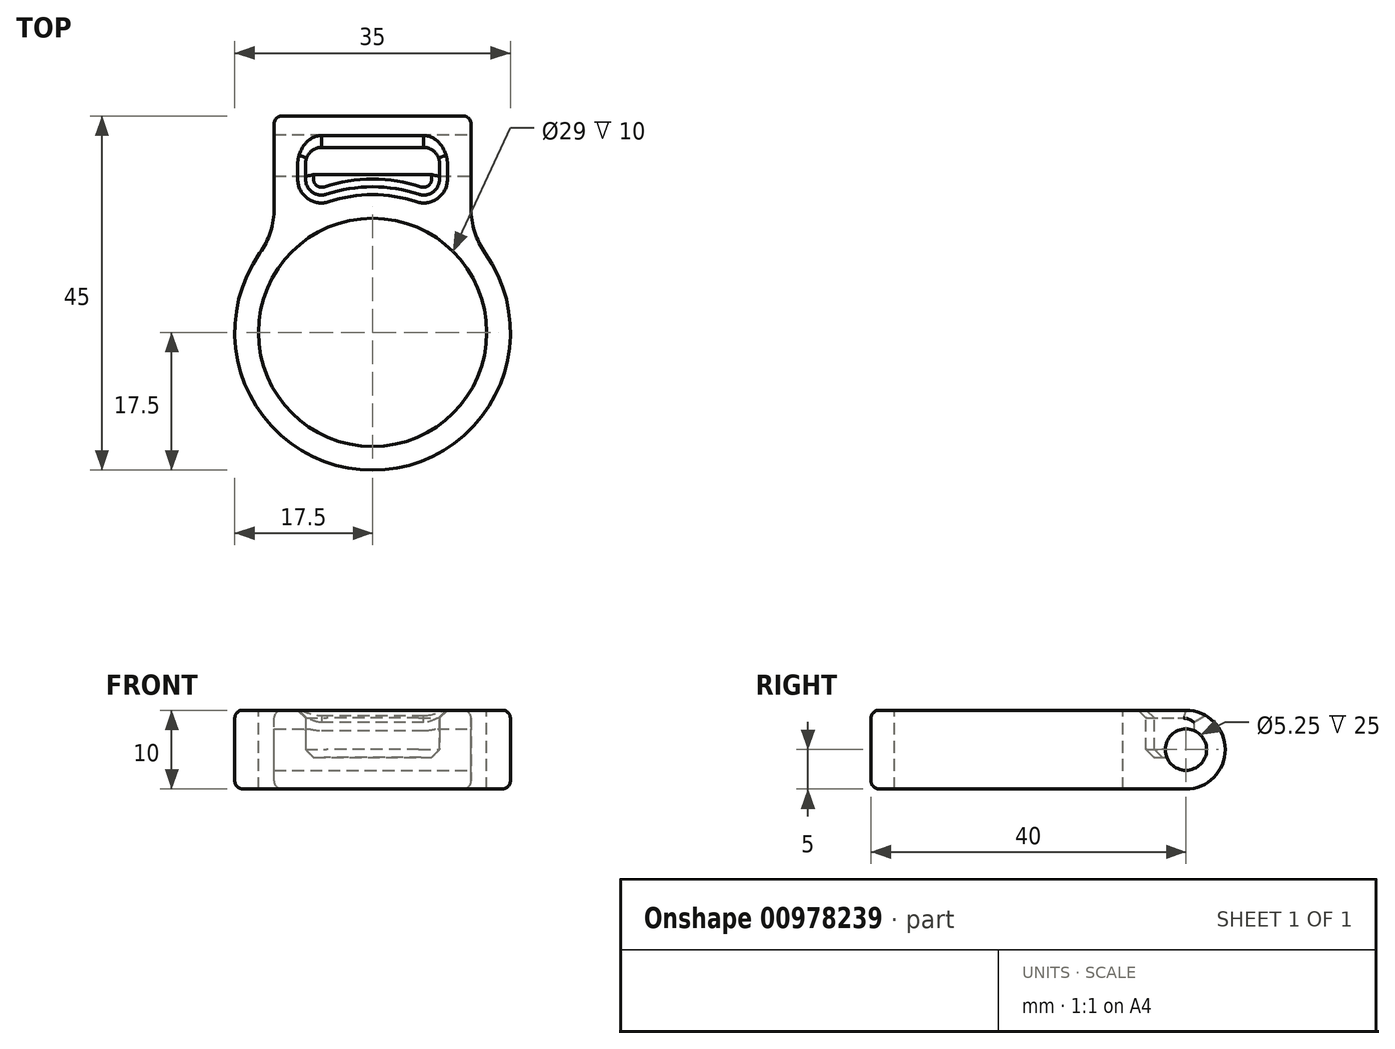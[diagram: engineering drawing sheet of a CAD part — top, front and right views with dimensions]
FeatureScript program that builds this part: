
annotation { "Feature Type Name" : "Feature", "Feature Type Description" : "" }
export const myFeature = defineFeature(function(context is Context, id is Id, definition is map)
    precondition{}
    {
        {
            var Q0;
            Q0=qCreatedBy(makeId("Top.planeOp"),FACE);
            var sketch = newSketch(context, id + "F0", { "sketchPlane" : qUnion([Q0])});
            skCircle(sketch, "E0", {"center": v(0, 0) * mm, "radius": 17.5 * mm});
            skLineSegment(sketch, "E1", {"start": v(0, 0) * mm, "end": v(0, 48.37) * mm, "construction": true});
            skLineSegment(sketch, "E2", {"start": v(0, 27.5) * mm, "end": v(-12.5, 27.5) * mm});
            skPoint(sketch, "E3", {"position": v(0, 17.5) * mm});
            skLineSegment(sketch, "E4.MirrorCS", {"start": v(0, 27.5) * mm, "end": v(12.5, 27.5) * mm});
            skLineSegment(sketch, "E5", {"start": v(-12.5, 27.5) * mm, "end": v(-12.5, 12.25) * mm});
            skLineSegment(sketch, "E6.MirrorCS", {"start": v(12.5, 27.5) * mm, "end": v(12.5, 12.25) * mm});
            skSolve(sketch);
        }
        {
            var Q0;
            {var subQ0=sQuery(id+"F0.wireOp",EDGE,"E0");var subQ1=makeQuery(id+"F0.imprint","INTERSECT",VERTEX,{"derivedFrom":[subQ0,sQuery(id+"F0.wireOp",EDGE,"E5")]});Q0=makeQuery(id+"F0.imprint","IMPRINT",FACE,{"disambiguationData":[TD([[makeQuery(id+"F0.imprint","IMPRINT",EDGE,{"disambiguationData":[TD([[subQ1,1.0]])],"derivedFrom":subQ0}),1.0]])]});}
            var Q1;
            Q1=makeQuery(id+"F0.imprint","IMPRINT",FACE,{"disambiguationData":[TD([[makeQuery(id+"F0.imprint","IMPRINT",EDGE,{"derivedFrom":sQuery(id+"F0.wireOp",EDGE,"E2")}),1.0]])]});
            extrude(context, id + "F1", {"entities" : qUnion([Q0, Q1]), "depth" : 10 * mm, "offsetDistance" : 25 * mm});
        }
        {
            var Q0;
            Q0=makeQuery(id+"F1.opExtrude","CAP_FACE",FACE,{"disambiguationData":[OSD([sQuery(id+"F0.wireOp",EDGE,"E0"),sQuery(id+"F0.wireOp",EDGE,"E2"),sQuery(id+"F0.wireOp",EDGE,"E4.MirrorCS"),sQuery(id+"F0.wireOp",EDGE,"E5"),sQuery(id+"F0.wireOp",EDGE,"E6.MirrorCS")])],"isStart":false});
            var sketch = newSketch(context, id + "F2", { "sketchPlane" : qUnion([Q0])});
            skCircle(sketch, "E7", {"center": v(0, 0) * mm, "radius": 14.5 * mm});
            skSolve(sketch);
        }
        {
            var Q0;
            Q0=makeQuery(id+"F2.imprint","IMPRINT",FACE,{"disambiguationData":[TD([[makeQuery(id+"F2.imprint","IMPRINT",EDGE,{"derivedFrom":sQuery(id+"F2.wireOp",EDGE,"E7")}),1.0]])]});
            extrude(context, id + "F3", {"entities" : qUnion([Q0]), "operationType" : NewBodyOperationType.REMOVE, "endBound" : BoundingType.THROUGH_ALL, "oppositeDirection" : true, "depth" : 25 * mm, "offsetDistance" : 25 * mm});
        }
        {
            var Q0;
            Q0=makeQuery(id+"F1.opExtrude","SWEPT_EDGE",EDGE,{"disambiguationData":[OSD([sQuery(id+"F0.wireOp",EDGE,"E0"),sQuery(id+"F0.wireOp",EDGE,"E5")])]});
            var Q1;
            Q1=makeQuery(id+"F1.opExtrude","SWEPT_EDGE",EDGE,{"disambiguationData":[OSD([sQuery(id+"F0.wireOp",EDGE,"E0"),sQuery(id+"F0.wireOp",EDGE,"E6.MirrorCS")])]});
            fillet(context, id + "F4", {"entities" : qUnion([Q0, Q1]), "radius" : 10 * mm, "tangentPropagation" : true, "allowEdgeOverflow" : false});
        }
        {
            var Q0;
            Q0=makeQuery(id+"F1.opExtrude","CAP_FACE",FACE,{"disambiguationData":[OSD([sQuery(id+"F0.wireOp",EDGE,"E0"),sQuery(id+"F0.wireOp",EDGE,"E2"),sQuery(id+"F0.wireOp",EDGE,"E4.MirrorCS"),sQuery(id+"F0.wireOp",EDGE,"E5"),sQuery(id+"F0.wireOp",EDGE,"E6.MirrorCS")])],"isStart":false});
            shell(context, id + "F5", {"entities" : qUnion([Q0]), "thickness" : 4 * mm});
        }
        {
            var Q0;
            Q0=makeQuery(id+"F1.opExtrude","CAP_EDGE",EDGE,{"disambiguationData":[OSD([sQuery(id+"F0.wireOp",EDGE,"E2"),sQuery(id+"F0.wireOp",EDGE,"E4.MirrorCS")])],"isStart":false});
            var Q1;
            Q1=makeQuery(id+"F1.opExtrude","CAP_EDGE",EDGE,{"disambiguationData":[OSD([sQuery(id+"F0.wireOp",EDGE,"E2"),sQuery(id+"F0.wireOp",EDGE,"E4.MirrorCS")])],"isStart":true});
            fillet(context, id + "F6", {"entities" : qUnion([Q0, Q1]), "radius" : 5 * mm, "tangentPropagation" : true, "allowEdgeOverflow" : false});
        }
        {
            var Q0;
            Q0=makeQuery(id+"F5.opShell","OFFSET_EDGE",EDGE,{"disambiguationData":[OSD([sQuery(id+"F0.wireOp",EDGE,"E2"),sQuery(id+"F0.wireOp",EDGE,"E5")])]});
            var Q1;
            Q1=makeQuery(id+"F5.opShell","OFFSET_EDGE",EDGE,{"disambiguationData":[OSD([sQuery(id+"F0.wireOp",EDGE,"E4.MirrorCS"),sQuery(id+"F0.wireOp",EDGE,"E6.MirrorCS")])]});
            var Q2;
            Q2=makeQuery(id+"F5.opShell","TWEAK_EDGE",EDGE,{"derivedFrom":[makeQuery(id+"F3.boolean.opBoolean","COPY",FACE,{"derivedFrom":makeQuery(id+"F3.opExtrude","SWEPT_FACE",FACE,{"disambiguationData":[OSD([sQuery(id+"F2.wireOp",EDGE,"E7")])]})}),makeQuery(id+"F1.opExtrude","SWEPT_FACE",FACE,{"disambiguationData":[OSD([sQuery(id+"F0.wireOp",EDGE,"E5")])]})]});
            var Q3;
            Q3=makeQuery(id+"F5.opShell","TWEAK_EDGE",EDGE,{"derivedFrom":[makeQuery(id+"F3.boolean.opBoolean","COPY",FACE,{"derivedFrom":makeQuery(id+"F3.opExtrude","SWEPT_FACE",FACE,{"disambiguationData":[OSD([sQuery(id+"F2.wireOp",EDGE,"E7")])]})}),makeQuery(id+"F1.opExtrude","SWEPT_FACE",FACE,{"disambiguationData":[OSD([sQuery(id+"F0.wireOp",EDGE,"E6.MirrorCS")])]})]});
            fillet(context, id + "F7", {"entities" : qUnion([Q0, Q1, Q2, Q3]), "radius" : 2 * mm, "tangentPropagation" : true, "allowEdgeOverflow" : false});
        }
        {
            var Q0;
            Q0=makeQuery(id+"F1.opExtrude","SWEPT_FACE",FACE,{"disambiguationData":[OSD([sQuery(id+"F0.wireOp",EDGE,"E6.MirrorCS")])]});
            var sketch = newSketch(context, id + "F8", { "sketchPlane" : qUnion([Q0])});
            skCircle(sketch, "E8", {"center": v(22.5, 5) * mm, "radius": 2.62 * mm});
            skSolve(sketch);
        }
        {
            var Q0;
            Q0=makeQuery(id+"F8.imprint","IMPRINT",FACE,{"disambiguationData":[TD([[makeQuery(id+"F8.imprint","IMPRINT",EDGE,{"derivedFrom":sQuery(id+"F8.wireOp",EDGE,"E8")}),1.0]])]});
            extrude(context, id + "F9", {"entities" : qUnion([Q0]), "operationType" : NewBodyOperationType.REMOVE, "endBound" : BoundingType.THROUGH_ALL, "oppositeDirection" : true, "depth" : 25 * mm, "offsetDistance" : 25 * mm});
        }
        {
            var Q0;
            Q0=makeQuery(id+"F5.opShell","OFFSET_EDGE",EDGE,{"disambiguationData":[OSD([sQuery(id+"F2.wireOp",EDGE,"E7")])]});
            chamfer(context, id + "F10", {"entities" : qUnion([Q0]), "width" : 1 * mm, "tangentPropagation" : true});
        }
        {
            var Q0;
            Q0=makeQuery(id+"F1.opExtrude","CAP_EDGE",EDGE,{"disambiguationData":[OSD([sQuery(id+"F0.wireOp",EDGE,"E0")])],"isStart":false});
            fillet(context, id + "F11", {"entities" : qUnion([Q0]), "radius" : 1 * mm, "tangentPropagation" : true, "allowEdgeOverflow" : false});
        }
    });
